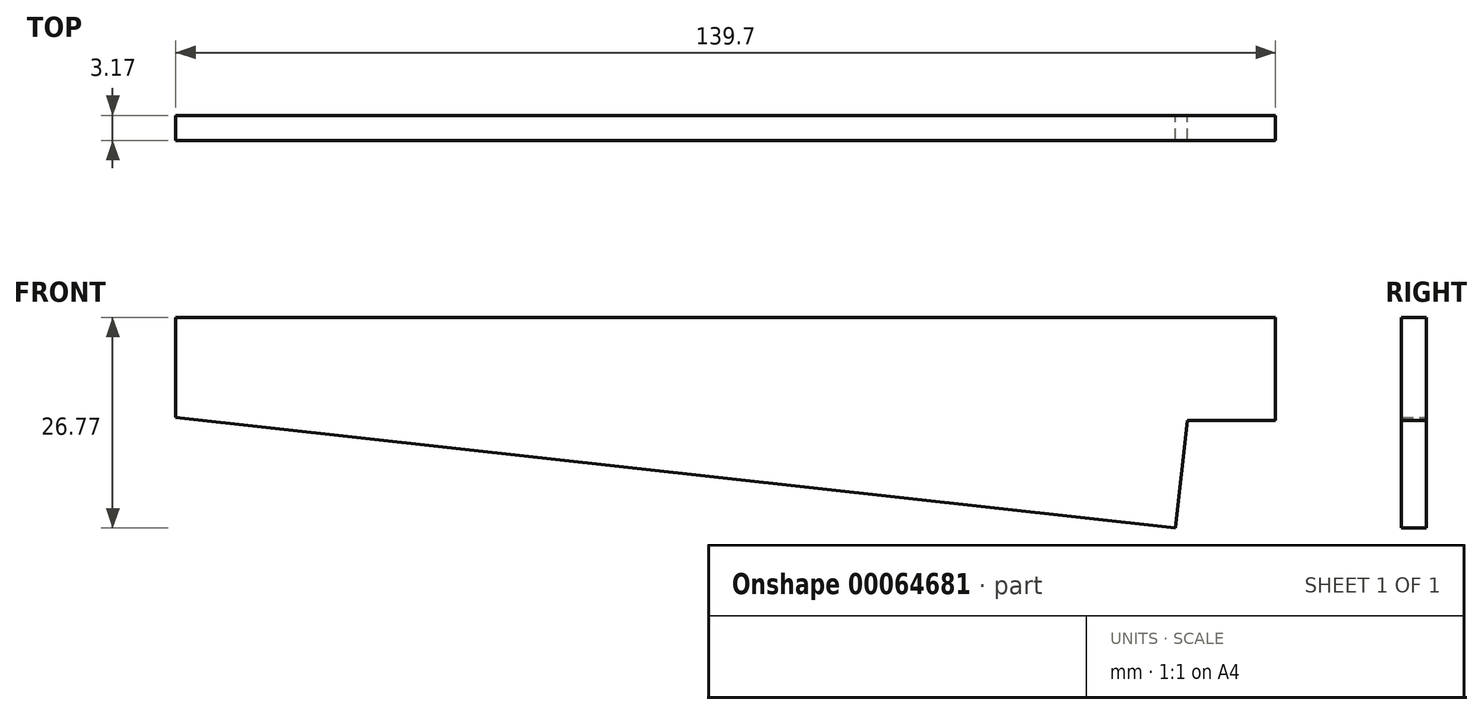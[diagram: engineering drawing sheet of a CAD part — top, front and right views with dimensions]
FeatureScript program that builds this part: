
annotation { "Feature Type Name" : "Feature", "Feature Type Description" : "" }
export const myFeature = defineFeature(function(context is Context, id is Id, definition is map)
    precondition{}
    {
        {
            var Q0;
            Q0=qCreatedBy(makeId("Front.planeOp"),FACE);
            var sketch = newSketch(context, id + "F0", { "sketchPlane" : qUnion([Q0])});
            skLineSegment(sketch, "E0", {"start": v(0, -8.93) * mm, "end": v(-139.7, -8.93) * mm});
            skLineSegment(sketch, "E1", {"start": v(-139.7, -8.93) * mm, "end": v(-139.7, -21.63) * mm});
            skLineSegment(sketch, "E2", {"start": v(-139.7, -21.63) * mm, "end": v(-12.7, -35.7) * mm});
            skLineSegment(sketch, "E3", {"start": v(0, -22.04) * mm, "end": v(0, -8.93) * mm});
            skLineSegment(sketch, "E4", {"start": v(-12.7, -35.7) * mm, "end": v(-11.19, -22.04) * mm});
            skLineSegment(sketch, "E5", {"start": v(-11.19, -22.04) * mm, "end": v(0, -22.04) * mm});
            skSolve(sketch);
        }
        {
            var Q0;
            Q0=makeQuery(id+"F0.imprint","IMPRINT",FACE,{"disambiguationData":[TD([[makeQuery(id+"F0.imprint","IMPRINT",EDGE,{"derivedFrom":sQuery(id+"F0.wireOp",EDGE,"E0")}),1.0]])]});
            extrude(context, id + "F1", {"entities" : qUnion([Q0]), "depth" : 3.17 * mm});
        }
    });
